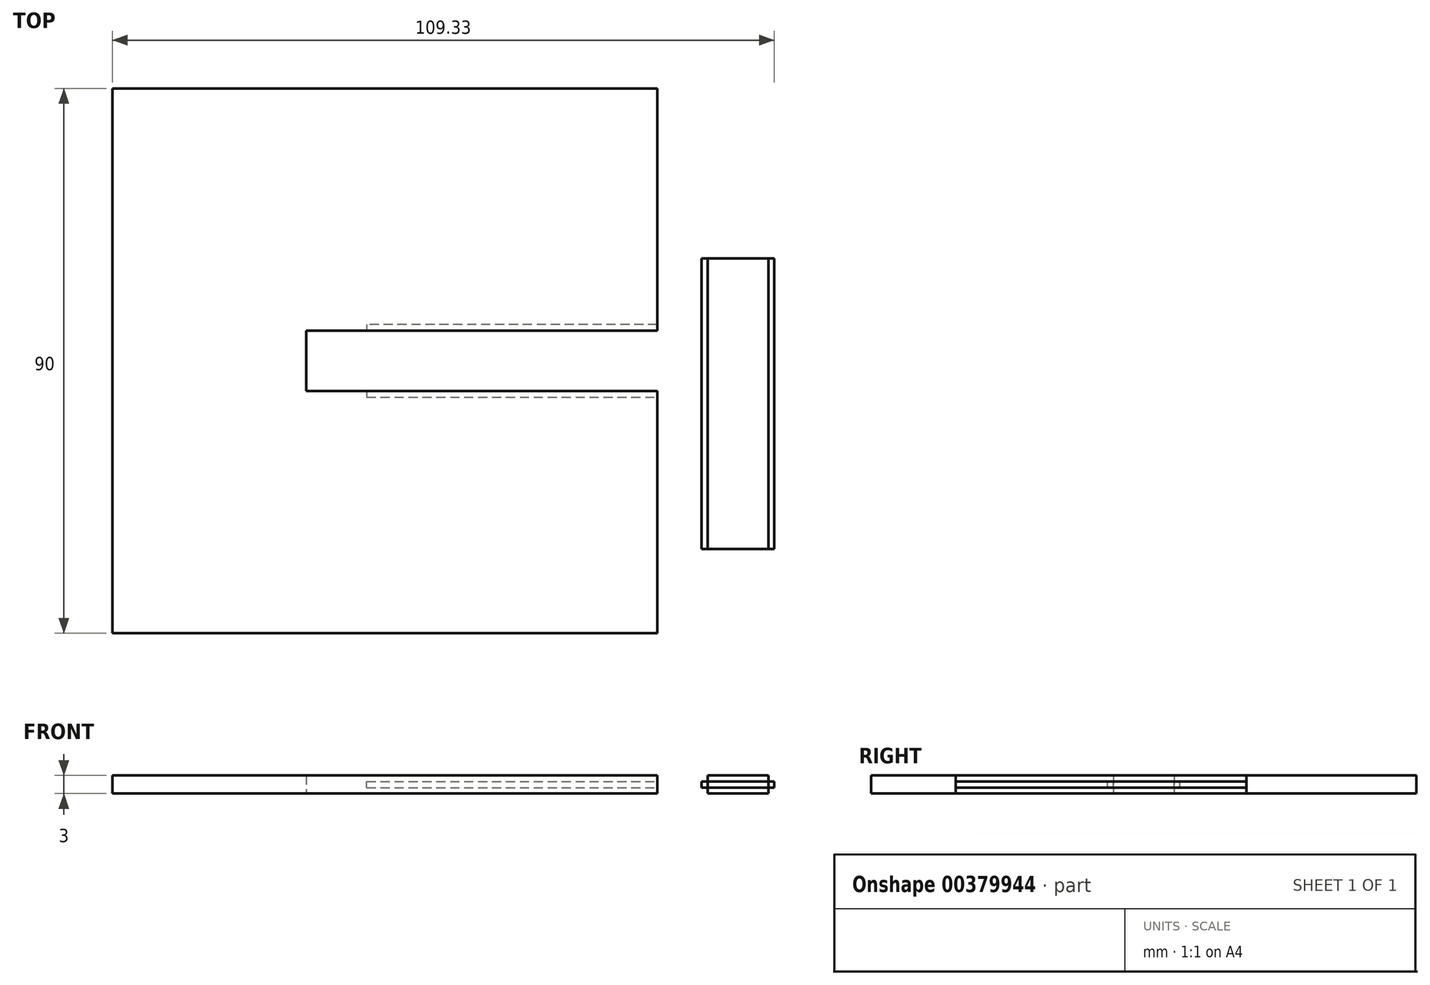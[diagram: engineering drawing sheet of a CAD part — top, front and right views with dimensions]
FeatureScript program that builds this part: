
annotation { "Feature Type Name" : "Feature", "Feature Type Description" : "" }
export const myFeature = defineFeature(function(context is Context, id is Id, definition is map)
    precondition{}
    {
        {
            var Q0;
            Q0=qCreatedBy(makeId("Top.planeOp"),FACE);
            var sketch = newSketch(context, id + "F0", { "sketchPlane" : qUnion([Q0])});
            skLineSegment(sketch, "E0.bottom", {"start": v(-36, 57.16) * mm, "end": v(54, 57.16) * mm});
            skLineSegment(sketch, "E0.top", {"start": v(-36, -32.84) * mm, "end": v(54, -32.84) * mm});
            skLineSegment(sketch, "E0.left", {"start": v(-36, 57.16) * mm, "end": v(-36, -32.84) * mm});
            skLineSegment(sketch, "E0.right", {"start": v(54, 57.16) * mm, "end": v(54, -32.84) * mm});
            skLineSegment(sketch, "E1.bottom", {"start": v(-4, 7.16) * mm, "end": v(54, 7.16) * mm});
            skLineSegment(sketch, "E1.top", {"start": v(-4, 17.16) * mm, "end": v(54, 17.16) * mm});
            skLineSegment(sketch, "E1.left", {"start": v(-4, 7.16) * mm, "end": v(-4, 17.16) * mm});
            skLineSegment(sketch, "E1.right", {"start": v(54, 7.16) * mm, "end": v(54, 17.16) * mm});
            skSolve(sketch);
        }
        {
            var Q0;
            {var subQ5=sQuery(id+"F0.wireOp",EDGE,"E1.right");Q0=makeQuery(id+"F0.imprint","IMPRINT",FACE,{"disambiguationData":[TD([[makeQuery(id+"F0.imprint","IMPRINT",EDGE,{"derivedFrom":subQ5}),1.0]])]});}
            var Q1;
            {var subQ1=sQuery(id+"F0.wireOp",EDGE,"E0.bottom");Q1=makeQuery(id+"F0.imprint","IMPRINT",FACE,{"disambiguationData":[TD([[makeQuery(id+"F0.imprint","IMPRINT",EDGE,{"derivedFrom":subQ1}),-1.0]])]});}
            extrude(context, id + "F1", {"entities" : qUnion([Q0, Q1]), "depth" : 3 * mm});
        }
        {
            var Q0;
            Q0=qCreatedBy(makeId("Top.planeOp"),FACE);
            var sketch = newSketch(context, id + "F2", { "sketchPlane" : qUnion([Q0])});
            skLineSegment(sketch, "E2.bottom", {"start": v(54, 18.16) * mm, "end": v(6, 18.16) * mm});
            skLineSegment(sketch, "E2.top", {"start": v(6, 6.16) * mm, "end": v(54, 6.16) * mm});
            skLineSegment(sketch, "E2.left", {"start": v(54, 18.16) * mm, "end": v(54, 6.16) * mm});
            skLineSegment(sketch, "E2.right", {"start": v(6, 18.16) * mm, "end": v(6, 6.16) * mm});
            skSolve(sketch);
        }
        {
            var Q0;
            Q0 = qSketchRegion(id + "F2", true);
            extrude(context, id + "F3", {"entities" : qUnion([Q0]), "endBound" : BoundingType.SYMMETRIC, "oppositeDirection" : true, "depth" : 1 * mm});
        }
        {
            var Q0;
            Q0=makeQuery(id+"F3.opExtrude","SWEPT_BODY",BODY,{"disambiguationData":[OSD([sQuery(id+"F2.wireOp",EDGE,"E2.bottom"),sQuery(id+"F2.wireOp",EDGE,"E2.top"),sQuery(id+"F2.wireOp",EDGE,"E2.left"),sQuery(id+"F2.wireOp",EDGE,"E2.right")])]});
            transform(context, id + "F4", {"entities" : qUnion([Q0]), "transformType" : TransformType.TRANSLATION_3D, "dx" : 0 * mm, "dy" : 0 * mm, "dz" : 1.5 * mm, "makeCopy" : false});
        }
        {
            var Q0;
            Q0=makeQuery(id+"F3.opExtrude","SWEPT_BODY",BODY,{"disambiguationData":[OSD([sQuery(id+"F2.wireOp",EDGE,"E2.bottom"),sQuery(id+"F2.wireOp",EDGE,"E2.top"),sQuery(id+"F2.wireOp",EDGE,"E2.left"),sQuery(id+"F2.wireOp",EDGE,"E2.right")])]});
            var Q1;
            Q1=makeQuery(id+"F1.opExtrude","SWEPT_BODY",BODY,{"disambiguationData":[OSD([sQuery(id+"F0.wireOp",EDGE,"E0.bottom"),sQuery(id+"F0.wireOp",EDGE,"E0.top"),sQuery(id+"F0.wireOp",EDGE,"E0.left"),sQuery(id+"F0.wireOp",EDGE,"E0.right"),sQuery(id+"F0.wireOp",EDGE,"E1.bottom"),sQuery(id+"F0.wireOp",EDGE,"E1.top"),sQuery(id+"F0.wireOp",EDGE,"E1.left")])]});
            booleanBodies(context, id + "F5", {"operationType" : BooleanOperationType.SUBTRACTION, "tools" : qUnion([Q0]), "targets" : qUnion([Q1])});
        }
        {
            var Q0;
            Q0=makeQuery(id+"F1.opExtrude","SWEPT_BODY",BODY,{"disambiguationData":[OSD([sQuery(id+"F0.wireOp",EDGE,"E0.right"),sQuery(id+"F0.wireOp",EDGE,"E1.bottom"),sQuery(id+"F0.wireOp",EDGE,"E1.top"),sQuery(id+"F0.wireOp",EDGE,"E1.right")])]});
            deleteBodies(context, id + "F6", {"entities" : qUnion([Q0])});
        }
        {
            var Q0;
            Q0=qCreatedBy(makeId("Top.planeOp"),FACE);
            var sketch = newSketch(context, id + "F7", { "sketchPlane" : qUnion([Q0])});
            skLineSegment(sketch, "E3.bottom", {"start": v(50.32, 29.09) * mm, "end": v(60.32, 29.09) * mm});
            skLineSegment(sketch, "E3.top", {"start": v(50.32, -18.91) * mm, "end": v(60.32, -18.91) * mm});
            skLineSegment(sketch, "E3.left", {"start": v(50.32, 29.09) * mm, "end": v(50.32, -18.91) * mm});
            skLineSegment(sketch, "E3.right", {"start": v(60.32, 29.09) * mm, "end": v(60.32, -18.91) * mm});
            skSolve(sketch);
        }
        {
            var Q0;
            Q0 = qSketchRegion(id + "F7", true);
            extrude(context, id + "F8", {"entities" : qUnion([Q0]), "depth" : 3 * mm});
        }
        {
            var Q0;
            Q0=makeQuery(id+"F8.opExtrude","CAP_FACE",FACE,{"disambiguationData":[OSD([sQuery(id+"F7.wireOp",EDGE,"E3.bottom"),sQuery(id+"F7.wireOp",EDGE,"E3.top"),sQuery(id+"F7.wireOp",EDGE,"E3.left"),sQuery(id+"F7.wireOp",EDGE,"E3.right")])],"isStart":true});
            var sketch = newSketch(context, id + "F9", { "sketchPlane" : qUnion([Q0])});
            skLineSegment(sketch, "E4.bottom", {"start": v(49.32, -29.09) * mm, "end": v(61.32, -29.09) * mm});
            skLineSegment(sketch, "E4.top", {"start": v(49.32, 18.91) * mm, "end": v(61.32, 18.91) * mm});
            skLineSegment(sketch, "E4.left", {"start": v(49.32, -29.09) * mm, "end": v(49.32, 18.91) * mm});
            skLineSegment(sketch, "E4.right", {"start": v(61.32, -29.09) * mm, "end": v(61.32, 18.91) * mm});
            skSolve(sketch);
        }
        {
            var Q0;
            Q0 = qSketchRegion(id + "F9", true);
            extrude(context, id + "F10", {"entities" : qUnion([Q0]), "depth" : 1 * mm});
        }
        {
            var Q0;
            Q0=makeQuery(id+"F10.opExtrude","SWEPT_BODY",BODY,{"disambiguationData":[OSD([sQuery(id+"F9.wireOp",EDGE,"E4.bottom"),sQuery(id+"F9.wireOp",EDGE,"E4.top"),sQuery(id+"F9.wireOp",EDGE,"E4.left"),sQuery(id+"F9.wireOp",EDGE,"E4.right")])]});
            transform(context, id + "F11", {"entities" : qUnion([Q0]), "transformType" : TransformType.TRANSLATION_3D, "dx" : 12 * mm, "dy" : 0 * mm, "dz" : 2 * mm, "makeCopy" : false});
        }
        {
            var Q0;
            Q0=makeQuery(id+"F8.opExtrude","SWEPT_BODY",BODY,{"disambiguationData":[OSD([sQuery(id+"F7.wireOp",EDGE,"E3.bottom"),sQuery(id+"F7.wireOp",EDGE,"E3.top"),sQuery(id+"F7.wireOp",EDGE,"E3.left"),sQuery(id+"F7.wireOp",EDGE,"E3.right")])]});
            transform(context, id + "F12", {"entities" : qUnion([Q0]), "transformType" : TransformType.TRANSLATION_3D, "dx" : 12 * mm, "dy" : 0 * mm, "dz" : 0 * mm, "makeCopy" : false});
        }
    });
